# Revit family: Shower-Wall-Bradley_Corp-HN200-VL-SR-SB
name_source: partatom
category: Plumbing Fixtures
revit_build: Autodesk Revit MEP 2012 (Build: 20110309_2315(x64)
units: mm (PartAtom-declared; Revit-internal decimal feet)

## types (86) — shared parameters
ADA Compliant = Yes
Assembly Code = D2010710
Buy American Act = To Be Determined
Cold Water Connection Diameter = 1"
Cold Water Connection Radius = 0"
Depth = 36 "
Description = Recess-Mounted ADA Compliant Wall Shower
Height = 80.627 "
Hot Water Connection Diameter = 1"
Hot Water Connection Radius = 0"
Installation Type = Wall Mounted
Manufacturer = Bradley Corporation
MasterFormat Number = 22 42 23
MasterFormat Title = Commercial Showers
Maximum Operating Pressure = 0.00 psi
Minimum Flow = 0 GPM
OmniClass Table 21 Number = 21-04 20 10 60
OmniClass Table 21 Title = Plumbing Fixtures
OmniClass Table 23 Number = 23-31 17 00
OmniClass Table 23 Title = Showers
Product Tech Data URL - English = http://bradleycorp.com
SVHC = Yes
Seat Material = Plastic - Bradley Corp - Polyethylene - White
Shower Panel Material = Metal - Bradley Corp - Stainless Steel
Showerhead Material = Metal - Bradley Corp - Chrome
Specifications URL = http://www.bradleycorp.com
URL = http://www.bradleycorp.com
Valve Material = Metal - Bradley Corp - Chrome
Version = 2.0
Width = 36 "
zero-valued in all types: CWFU, HWFU, Percentage of Recycled Content

## per-type parameters (varying)
| type | Air Metering Valve | CALC_ASTT | CALC_EqPlate | CALC_EqTMV | Deluxe Showerhead with Ball Joint | Economy Soft Flow Showerhead with Ball Joint | Equa-Flo HD Pressure Balancing Valve | Equa-Flo Pressure Balancing Valve | Infrared Metering Valve | Lockable Ball Joint | Model | Optional 1.5 GPM Flow Control | Recessed Soap Dish | Severe Service Showerhead | Single Compression Valve with Lever Handle | Soap Container in Panel with Liquid Soap Valve | Standard Showerhead | Thermostatic Mixing Valve | TouchTime Metering Valve | Type Comments |
| Hot/Tempered and Cold Supplies | No | No | No | No | No | No | No | No | No | No | - | No | No | No | No | No | No | No | No | - |
| HN200-VL-SR-SB-EF-S-CS | No | No | Yes | No | No | No | No | Yes | No | No | HN200-VL-SR-SB | No | Yes | No | No | Yes | Yes | No | No | Recess-Mounted ADA Compliant Wall Shower with Equa-Flo Pressure Balancing Valve and Standard Showerhead and Soap Container in Panel with Liquid Soap Valve |
| HN200-VL-SR-SB-HD-S-CS | No | No | Yes | Yes | No | No | Yes | No | No | No | HN200-VL-SR-SB | No | Yes | No | No | Yes | Yes | No | No | Recess-Mounted ADA Compliant Wall Shower with Equa-Flo HD Pressure Balancing Valve and Standard Showerhead and Soap Container in Panel with Liquid Soap Valve |
| HN200-VL-SR-SB-TMV-S-CS | No | No | Yes | Yes | No | No | No | No | No | No | HN200-VL-SR-SB | No | Yes | No | No | Yes | Yes | Yes | No | Recess-Mounted ADA Compliant Wall Shower with Thermostatic Mixing Valve and Standard Showerhead and Soap Container in Panel with Liquid Soap Valve |
| HN200-VL-SR-SB-EF-SX-CS | No | No | Yes | No | No | No | No | Yes | No | No | HN200-VL-SR-SB | No | Yes | Yes | No | Yes | No | No | No | Recess-Mounted ADA Compliant Wall Shower with Equa-Flo Pressure Balancing Valve and Severe Service Showerhead and Soap Container in Panel with Liquid Soap Valve |
| HN200-VL-SR-SB-EF-SX-G-CS | No | No | Yes | No | No | No | No | Yes | No | No | HN200-VL-SR-SB | Yes | Yes | Yes | No | Yes | No | No | No | Recess-Mounted ADA Compliant Wall Shower with Equa-Flo Pressure Balancing Valve and Severe Service Showerhead with optional 1.5GPM Flow Control and Soap Container in Panel with Liquid Soap Valve |
| HN200-VL-SR-SB-HD-SX-CS | No | No | Yes | Yes | No | No | Yes | No | No | No | HN200-VL-SR-SB | No | Yes | Yes | No | Yes | No | No | No | Recess-Mounted ADA Compliant Wall Shower with Equa-Flo HD Pressure Balancing Valve and Severe Service Showerhead and Soap Container in Panel with Liquid Soap Valve |
| HN200-VL-SR-SB-HD-SX-G-CS | No | No | Yes | Yes | No | No | Yes | No | No | No | HN200-VL-SR-SB | Yes | Yes | Yes | No | Yes | No | No | No | Recess-Mounted ADA Compliant Wall Shower with Equa-Flo HD Pressure Balancing Valve and Severe Service Showerhead with optional 1.5GPM Flow Control and Soap Container in Panel with Liquid Soap Valve |
| HN200-VL-SR-SB-TMV-SX-CS | No | No | Yes | Yes | No | No | No | No | No | No | HN200-VL-SR-SB | No | Yes | Yes | No | Yes | No | Yes | No | Recess-Mounted ADA Compliant Wall Shower with Thermostatic Mixing Valve and Severe Service Showerhead and Soap Container in Panel with Liquid Soap Valve |
| HN200-VL-SR-SB-TMV-SX-G-CS | No | No | Yes | Yes | No | No | No | No | No | No | HN200-VL-SR-SB | Yes | Yes | Yes | No | Yes | No | Yes | No | Recess-Mounted ADA Compliant Wall Shower with Thermostatic Mixing Valve and Severe Service Showerhead with optional 1.5GPM Flow Control and Soap Container in Panel with Liquid Soap Valve |
| HN200-VL-SR-SB-EF-SF-CS | No | No | Yes | No | Yes | No | No | Yes | No | No | HN200-VL-SR-SB | No | Yes | No | No | Yes | No | No | No | Recess-Mounted ADA Compliant Wall Shower with Equa-Flo Pressure Balancing Valve and Deluxe Showerhead with Ball Joint and Soap Container in Panel with Liquid Soap Valve |
| HN200-VL-SR-SB-EF-SF-LBJ-CS | No | No | Yes | No | Yes | No | No | Yes | No | Yes | HN200-VL-SR-SB | No | Yes | No | No | Yes | No | No | No | Recess-Mounted ADA Compliant Wall Shower with Equa-Flo Pressure Balancing Valve and Deluxe Showerhead with Ball Joint with optional Lockable Ball Joint and Soap Container in Panel with Liquid Soap Valve |
| HN200-VL-SR-SB-HD-SF-CS | No | No | Yes | Yes | Yes | No | Yes | No | No | No | HN200-VL-SR-SB | No | Yes | No | No | Yes | No | No | No | Recess-Mounted ADA Compliant Wall Shower with Equa-Flo HD Pressure Balancing Valve and Deluxe Showerhead with Ball Joint and Soap Container in Panel with Liquid Soap Valve |
| HN200-VL-SR-SB-HD-SF-LBJ-CS | No | No | Yes | Yes | Yes | No | Yes | No | No | Yes | HN200-VL-SR-SB | No | Yes | No | No | Yes | No | No | No | Recess-Mounted ADA Compliant Wall Shower with Equa-Flo HD Pressure Balancing Valve and Deluxe Showerhead with Ball Joint with optional Lockable Ball Joint and Soap Container in Panel with Liquid Soap Valve |
| HN200-VL-SR-SB-TMV-SF-CS | No | No | Yes | Yes | Yes | No | No | No | No | No | HN200-VL-SR-SB | No | Yes | No | No | Yes | No | Yes | No | Recess-Mounted ADA Compliant Wall Shower with Thermostatic Mixing Valve and Deluxe Showerhead with Ball Joint and Soap Container in Panel with Liquid Soap Valve |
| HN200-VL-SR-SB-TMV-SF-LBJ-CS | No | No | Yes | Yes | Yes | No | No | No | No | Yes | HN200-VL-SR-SB | No | Yes | No | No | Yes | No | Yes | No | Recess-Mounted ADA Compliant Wall Shower with Thermostatic Mixing Valve and Deluxe Showerhead with Ball Joint with optional Lockable Ball Joint and Soap Container in Panel with Liquid Soap Valve |
| HN200-VL-SR-SB-EF-ES-CS | No | No | Yes | No | No | Yes | No | Yes | No | No | HN200-VL-SR-SB | No | Yes | No | No | Yes | No | No | No | Recess-Mounted ADA Compliant Wall Shower with Equa-Flo Pressure Balancing Valve and Economy Soft Flow Showerhead with Ball Joint and Soap Container in Panel with Liquid Soap Valve |
| HN200-VL-SR-SB-HD-ES-CS | No | No | Yes | Yes | No | Yes | Yes | No | No | No | HN200-VL-SR-SB | No | Yes | No | No | Yes | No | No | No | Recess-Mounted ADA Compliant Wall Shower with Equa-Flo HD Pressure Balancing Valve and Economy Soft Flow Showerhead with Ball Joint and Soap Container in Panel with Liquid Soap Valve |
| HN200-VL-SR-SB-TMV-ES-CS | No | No | Yes | Yes | No | Yes | No | No | No | No | HN200-VL-SR-SB | No | Yes | No | No | Yes | No | Yes | No | Recess-Mounted ADA Compliant Wall Shower with Thermostatic Mixing Valve and Economy Soft Flow Showerhead with Ball Joint and Soap Container in Panel with Liquid Soap Valve |
| HN200-VL-SR-SB-EF-S | No | No | Yes | No | No | No | No | Yes | No | No | HN200-VL-SR-SB | No | Yes | No | No | No | Yes | No | No | Recess-Mounted ADA Compliant Wall Shower with Equa-Flo Pressure Balancing Valve and Standard Showerhead and Recessed Soap Dish |
| HN200-VL-SR-SB-HD-S | No | No | Yes | Yes | No | No | Yes | No | No | No | HN200-VL-SR-SB | No | Yes | No | No | No | Yes | No | No | Recess-Mounted ADA Compliant Wall Shower with Equa-Flo HD Pressure Balancing Valve and Standard Showerhead and Recessed Soap Dish |
| HN200-VL-SR-SB-TMV-S | No | No | Yes | Yes | No | No | No | No | No | No | HN200-VL-SR-SB | No | Yes | No | No | No | Yes | Yes | No | Recess-Mounted ADA Compliant Wall Shower with Thermostatic Mixing Valve and Standard Showerhead and Recessed Soap Dish |
| HN200-VL-SR-SB-EF-SX | No | No | Yes | No | No | No | No | Yes | No | No | HN200-VL-SR-SB | No | Yes | Yes | No | No | No | No | No | Recess-Mounted ADA Compliant Wall Shower with Equa-Flo Pressure Balancing Valve and Severe Service Showerhead and Recessed Soap Dish |
| HN200-VL-SR-SB-EF-SX-G | No | No | Yes | No | No | No | No | Yes | No | No | HN200-VL-SR-SB | Yes | Yes | Yes | No | No | No | No | No | Recess-Mounted ADA Compliant Wall Shower with Equa-Flo Pressure Balancing Valve and Severe Service Showerhead with optional 1.5GPM Flow Control and Recessed Soap Dish |
| HN200-VL-SR-SB-HD-SX | No | No | Yes | Yes | No | No | Yes | No | No | No | HN200-VL-SR-SB | No | Yes | Yes | No | No | No | No | No | Recess-Mounted ADA Compliant Wall Shower with Equa-Flo HD Pressure Balancing Valve and Severe Service Showerhead and Recessed Soap Dish |
| HN200-VL-SR-SB-HD-SX-G | No | No | Yes | Yes | No | No | Yes | No | No | No | HN200-VL-SR-SB | Yes | Yes | Yes | No | No | No | No | No | Recess-Mounted ADA Compliant Wall Shower with Equa-Flo HD Pressure Balancing Valve and Severe Service Showerhead with optional 1.5GPM Flow Control and Recessed Soap Dish |
| HN200-VL-SR-SB-TMV-SX | No | No | Yes | Yes | No | No | No | No | No | No | HN200-VL-SR-SB | No | Yes | Yes | No | No | No | Yes | No | Recess-Mounted ADA Compliant Wall Shower with Thermostatic Mixing Valve and Severe Service Showerhead and Recessed Soap Dish |
| HN200-VL-SR-SB-TMV-SX-G | No | No | Yes | Yes | No | No | No | No | No | No | HN200-VL-SR-SB | Yes | Yes | Yes | No | No | No | Yes | No | Recess-Mounted ADA Compliant Wall Shower with Thermostatic Mixing Valve and Severe Service Showerhead with optional 1.5GPM Flow Control and Recessed Soap Dish |
| HN200-VL-SR-SB-EF-SF | No | No | Yes | No | Yes | No | No | Yes | No | No | HN200-VL-SR-SB | No | Yes | No | No | No | No | No | No | Recess-Mounted ADA Compliant Wall Shower with Equa-Flo Pressure Balancing Valve and Deluxe Showerhead with Ball Joint and Recessed Soap Dish |
| HN200-VL-SR-SB-EF-SF-LBJ | No | No | Yes | No | Yes | No | No | Yes | No | Yes | HN200-VL-SR-SB | No | Yes | No | No | No | No | No | No | Recess-Mounted ADA Compliant Wall Shower with Equa-Flo Pressure Balancing Valve and Deluxe Showerhead with Ball Joint with optional Lockable Ball Joint and Recessed Soap Dish |
| HN200-VL-SR-SB-HD-SF | No | No | Yes | Yes | Yes | No | Yes | No | No | No | HN200-VL-SR-SB | No | Yes | No | No | No | No | No | No | Recess-Mounted ADA Compliant Wall Shower with Equa-Flo HD Pressure Balancing Valve and Deluxe Showerhead with Ball Joint and Recessed Soap Dish |
| HN200-VL-SR-SB-HD-SF-LBJ | No | No | Yes | Yes | Yes | No | Yes | No | No | Yes | HN200-VL-SR-SB | No | Yes | No | No | No | No | No | No | Recess-Mounted ADA Compliant Wall Shower with Equa-Flo HD Pressure Balancing Valve and Deluxe Showerhead with Ball Joint with optional Lockable Ball Joint and Recessed Soap Dish |
| HN200-VL-SR-SB-TMV-SF | No | No | Yes | Yes | Yes | No | No | No | No | No | HN200-VL-SR-SB | No | Yes | No | No | No | No | Yes | No | Recess-Mounted ADA Compliant Wall Shower with Thermostatic Mixing Valve and Deluxe Showerhead with Ball Joint and Recessed Soap Dish |
| HN200-VL-SR-SB-TMV-SF-LBJ | No | No | Yes | Yes | Yes | No | No | No | No | Yes | HN200-VL-SR-SB | No | Yes | No | No | No | No | Yes | No | Recess-Mounted ADA Compliant Wall Shower with Thermostatic Mixing Valve and Deluxe Showerhead with Ball Joint with optional Lockable Ball Joint and Recessed Soap Dish |
| HN200-VL-SR-SB-EF-ES | No | No | Yes | No | No | Yes | No | Yes | No | No | HN200-VL-SR-SB | No | Yes | No | No | No | No | No | No | Recess-Mounted ADA Compliant Wall Shower with Equa-Flo Pressure Balancing Valve and Economy Soft Flow Showerhead with Ball Joint and Recessed Soap Dish |
| HN200-VL-SR-SB-HD-ES | No | No | Yes | Yes | No | Yes | Yes | No | No | No | HN200-VL-SR-SB | No | Yes | No | No | No | No | No | No | Recess-Mounted ADA Compliant Wall Shower with Equa-Flo HD Pressure Balancing Valve and Economy Soft Flow Showerhead with Ball Joint and Recessed Soap Dish |
| HN200-VL-SR-SB-TMV-ES | No | No | Yes | Yes | No | Yes | No | No | No | No | HN200-VL-SR-SB | No | Yes | No | No | No | No | Yes | No | Recess-Mounted ADA Compliant Wall Shower with Thermostatic Mixing Valve and Economy Soft Flow Showerhead with Ball Joint and Recessed Soap Dish |
| Single Tempered/Cold Supply | No | No | No | No | No | No | No | No | No | No | - | No | No | No | No | No | No | No | No | - |
| HN200-VL-SR-SB-AZ-S-CS | No | No | No | No | No | No | No | No | Yes | No | HN200-VL-SR-SB | No | Yes | No | No | Yes | Yes | No | No | Recess-Mounted ADA Compliant Wall Shower with Infrared Metering Valve and Standard Showerhead and Soap Container in Panel with Liquid Soap Valve |
| HN200-VL-SR-SB-AZ-SX-CS | No | No | No | No | No | No | No | No | Yes | No | HN200-VL-SR-SB | No | Yes | Yes | No | Yes | No | No | No | Recess-Mounted ADA Compliant Wall Shower with Infrared Metering Valve and Severe Service Showerhead and Soap Container in Panel with Liquid Soap Valve |
| HN200-VL-SR-SB-AZ-SX-G-CS | No | No | No | No | No | No | No | No | Yes | No | HN200-VL-SR-SB | Yes | Yes | Yes | No | Yes | No | No | No | Recess-Mounted ADA Compliant Wall Shower with Infrared Metering Valve and Severe Service Showerhead with optional 1.5GPM Flow Control and Soap Container in Panel with Liquid Soap Valve |
| HN200-VL-SR-SB-AZ-SF-CS | No | No | No | No | Yes | No | No | No | Yes | No | HN200-VL-SR-SB | No | Yes | No | No | Yes | No | No | No | Recess-Mounted ADA Compliant Wall Shower with Infrared Metering Valve and Deluxe Showerhead with Ball Joint and Soap Container in Panel with Liquid Soap Valve |
| HN200-VL-SR-SB-AZ-SF-LBJ-CS | No | No | No | No | Yes | No | No | No | Yes | Yes | HN200-VL-SR-SB | No | Yes | No | No | Yes | No | No | No | Recess-Mounted ADA Compliant Wall Shower with Infrared Metering Valve and Deluxe Showerhead with Ball Joint with optional Lockable Ball Joint and Soap Container in Panel with Liquid Soap Valve |
| HN200-VL-SR-SB-AZ-ES-CS | No | No | No | No | No | Yes | No | No | Yes | No | HN200-VL-SR-SB | No | Yes | No | No | Yes | No | No | No | Recess-Mounted ADA Compliant Wall Shower with Infrared Metering Valve and Economy Soft Flow Showerhead with Ball Joint and Soap Container in Panel with Liquid Soap Valve |
| HN200-VL-SR-SB-AST-S-CS | Yes | Yes | No | No | No | No | No | No | No | No | HN200-VL-SR-SB | No | Yes | No | No | Yes | Yes | No | No | Recess-Mounted ADA Compliant Wall Shower with Air Metering Valve and Standard Showerhead and Soap Container in Panel with Liquid Soap Valve |
| HN200-VL-SR-SB-AST-SX-CS | Yes | Yes | No | No | No | No | No | No | No | No | HN200-VL-SR-SB | No | Yes | Yes | No | Yes | No | No | No | Recess-Mounted ADA Compliant Wall Shower with Air Metering Valve and Severe Service Showerhead and Soap Container in Panel with Liquid Soap Valve |
| HN200-VL-SR-SB-AST-SX-G-CS | Yes | Yes | No | No | No | No | No | No | No | No | HN200-VL-SR-SB | Yes | Yes | Yes | No | Yes | No | No | No | Recess-Mounted ADA Compliant Wall Shower with Air Metering Valve and Severe Service Showerhead with optional 1.5GPM Flow Control and Soap Container in Panel with Liquid Soap Valve |
| HN200-VL-SR-SB-AST-SF-CS | Yes | Yes | No | No | Yes | No | No | No | No | No | HN200-VL-SR-SB | No | Yes | No | No | Yes | No | No | No | Recess-Mounted ADA Compliant Wall Shower with Air Metering Valve and Deluxe Showerhead with Ball Joint and Soap Container in Panel with Liquid Soap Valve |
| HN200-VL-SR-SB-AST-SF-LBJ-CS | Yes | Yes | No | No | Yes | No | No | No | No | Yes | HN200-VL-SR-SB | No | Yes | No | No | Yes | No | No | No | Recess-Mounted ADA Compliant Wall Shower with Air Metering Valve and Deluxe Showerhead with Ball Joint with optional Lockable Ball Joint and Soap Container in Panel with Liquid Soap Valve |
| HN200-VL-SR-SB-AST-ES-CS | Yes | Yes | No | No | No | Yes | No | No | No | No | HN200-VL-SR-SB | No | Yes | No | No | Yes | No | No | No | Recess-Mounted ADA Compliant Wall Shower with Air Metering Valve and Economy Soft Flow Showerhead with Ball Joint and Soap Container in Panel with Liquid Soap Valve |
| HN200-VL-SR-SB-SVL-S-CS | No | No | No | No | No | No | No | No | No | No | HN200-VL-SR-SB | No | Yes | No | Yes | Yes | Yes | No | No | Recess-Mounted ADA Compliant Wall Shower with Single Compression Valve and Standard Showerhead and Soap Container in Panel with Liquid Soap Valve |
| HN200-VL-SR-SB-SVL-SX-CS | No | No | No | No | No | No | No | No | No | No | HN200-VL-SR-SB | No | Yes | Yes | Yes | Yes | No | No | No | Recess-Mounted ADA Compliant Wall Shower with Single Compression Valve and Severe Service Showerhead and Soap Container in Panel with Liquid Soap Valve |
| HN200-VL-SR-SB-SVL-SX-G-CS | No | No | No | No | No | No | No | No | No | No | HN200-VL-SR-SB | Yes | Yes | Yes | Yes | Yes | No | No | No | Recess-Mounted ADA Compliant Wall Shower with Single Compression Valve and Severe Service Showerhead with optional 1.5GPM Flow Control and Soap Container in Panel with Liquid Soap Valve |
| HN200-VL-SR-SB-SVL-SF-CS | No | No | No | No | Yes | No | No | No | No | No | HN200-VL-SR-SB | No | Yes | No | Yes | Yes | No | No | No | Recess-Mounted ADA Compliant Wall Shower with Single Compression Valve and Deluxe Showerhead with Ball Joint and Soap Container in Panel with Liquid Soap Valve |
| HN200-VL-SR-SB-SVL-SF-LBJ-CS | No | No | No | No | Yes | No | No | No | No | Yes | HN200-VL-SR-SB | No | Yes | No | Yes | Yes | No | No | No | Recess-Mounted ADA Compliant Wall Shower with Single Compression Valve and Deluxe Showerhead with Ball Joint with optional Lockable Ball Joint and Soap Container in Panel with Liquid Soap Valve |
| HN200-VL-SR-SB-SVL-ES-CS | No | No | No | No | No | Yes | No | No | No | No | HN200-VL-SR-SB | No | Yes | No | Yes | Yes | No | No | No | Recess-Mounted ADA Compliant Wall Shower with Single Compression Valve and Economy Soft Flow Showerhead wiht Ball Joint and Soap Container in Panel with Liquid Soap Valve |
| HN200-VL-SR-SB-TT-S-CS | No | Yes | No | No | No | No | No | No | No | No | HN200-VL-SR-SB | No | Yes | No | No | Yes | Yes | No | Yes | Recess-Mounted ADA Compliant Wall Shower with TouchTime÷ Metering Valve and Standard Showerhead and Soap Container in Panel with Liquid Soap Valve |
| HN200-VL-SR-SB-TT-SX-CS | No | Yes | No | No | No | No | No | No | No | No | HN200-VL-SR-SB | No | Yes | Yes | No | Yes | No | No | Yes | Recess-Mounted ADA Compliant Wall Shower with TouchTime÷ Metering Valve and Severe Service Showerhead and Soap Container in Panel with Liquid Soap Valve |
| HN200-VL-SR-SB-TT-SX-G-CS | No | Yes | No | No | No | No | No | No | No | No | HN200-VL-SR-SB | Yes | Yes | Yes | No | Yes | No | No | Yes | Recess-Mounted ADA Compliant Wall Shower with TouchTime÷ Metering Valve and Severe Service Showerhead with optional 1.5GPM Flow Control and Soap Container in Panel with Liquid Soap Valve |
| HN200-VL-SR-SB-TT-SF-CS | No | Yes | No | No | Yes | No | No | No | No | No | HN200-VL-SR-SB | No | Yes | No | No | Yes | No | No | Yes | Recess-Mounted ADA Compliant Wall Shower with TouchTime÷ Metering Valve and Deluxe Showerhead with Ball Joint and Soap Container in Panel with Liquid Soap Valve |
| HN200-VL-SR-SB-TT-SF-LBJ-CS | No | Yes | No | No | Yes | No | No | No | No | Yes | HN200-VL-SR-SB | No | Yes | No | No | Yes | No | No | Yes | Recess-Mounted ADA Compliant Wall Shower with TouchTime÷ Metering Valve and Deluxe Showerhead with Ball Joint with optional Lockable Ball Joint and Soap Container in Panel with Liquid Soap Valve |
| HN200-VL-SR-SB-TT-ES-CS | No | Yes | No | No | No | Yes | No | No | No | No | HN200-VL-SR-SB | No | Yes | No | No | Yes | No | No | Yes | Recess-Mounted ADA Compliant Wall Shower with TouchTime÷ Metering Valve and Economy Soft Flow Showerhead wiht Ball Joint and Soap Container in Panel with Liquid Soap Valve |
| HN200-VL-SR-SB-AZ-S | No | No | No | No | No | No | No | No | Yes | No | HN200-VL-SR-SB | No | Yes | No | No | No | Yes | No | No | Recess-Mounted ADA Compliant Wall Shower with Infrared Metering Valve and Standard Showerhead and Recessed Soap Dish |
| HN200-VL-SR-SB-AZ-SX | No | No | No | No | No | No | No | No | Yes | No | HN200-VL-SR-SB | No | Yes | Yes | No | No | No | No | No | Recess-Mounted ADA Compliant Wall Shower with Infrared Metering Valve and Severe Service Showerhead and Recessed Soap Dish |
| HN200-VL-SR-SB-AZ-SX-G | No | No | No | No | No | No | No | No | Yes | No | HN200-VL-SR-SB | Yes | Yes | Yes | No | No | No | No | No | Recess-Mounted ADA Compliant Wall Shower with Infrared Metering Valve and Severe Service Showerhead with optional 1.5GPM Flow Control and Recessed Soap Dish |
| HN200-VL-SR-SB-AZ-SF | No | No | No | No | Yes | No | No | No | Yes | No | HN200-VL-SR-SB | No | Yes | No | No | No | No | No | No | Recess-Mounted ADA Compliant Wall Shower with Infrared Metering Valve and Deluxe Showerhead with Ball Joint and Recessed Soap Dish |
| HN200-VL-SR-SB-AZ-SF-LBJ | No | No | No | No | Yes | No | No | No | Yes | Yes | HN200-VL-SR-SB | No | Yes | No | No | No | No | No | No | Recess-Mounted ADA Compliant Wall Shower with Infrared Metering Valve and Deluxe Showerhead with Ball Joint with optional Lockable Ball Joint and Recessed Soap Dish |
| HN200-VL-SR-SB-AZ-ES | No | No | No | No | No | Yes | No | No | Yes | No | HN200-VL-SR-SB | No | Yes | No | No | No | No | No | No | Recess-Mounted ADA Compliant Wall Shower with Infrared Metering Valve and Economy Soft Flow Showerhead with Ball Joint and Recessed Soap Dish |
| HN200-VL-SR-SB-AST-S | Yes | Yes | No | No | No | No | No | No | No | No | HN200-VL-SR-SB | No | Yes | No | No | No | Yes | No | No | Recess-Mounted ADA Compliant Wall Shower with Air Metering Valve and Standard Showerhead and Recessed Soap Dish |
| HN200-VL-SR-SB-AST-SX | Yes | Yes | No | No | No | No | No | No | No | No | HN200-VL-SR-SB | No | Yes | Yes | No | No | No | No | No | Recess-Mounted ADA Compliant Wall Shower with Air Metering Valve and Severe Service Showerhead and Recessed Soap Dish |
| HN200-VL-SR-SB-AST-SX-G | Yes | Yes | No | No | No | No | No | No | No | No | HN200-VL-SR-SB | Yes | Yes | Yes | No | No | No | No | No | Recess-Mounted ADA Compliant Wall Shower with Air Metering Valve and Severe Service Showerhead with optional 1.5GPM Flow Control and Recessed Soap Dish |
| HN200-VL-SR-SB-AST-SF | Yes | Yes | No | No | Yes | No | No | No | No | No | HN200-VL-SR-SB | No | Yes | No | No | No | No | No | No | Recess-Mounted ADA Compliant Wall Shower with Air Metering Valve and Deluxe Showerhead with Ball Joint and Recessed Soap Dish |
| HN200-VL-SR-SB-AST-SF-LBJ | Yes | Yes | No | No | Yes | No | No | No | No | Yes | HN200-VL-SR-SB | No | Yes | No | No | No | No | No | No | Recess-Mounted ADA Compliant Wall Shower with Air Metering Valve and Deluxe Showerhead with Ball Joint with optional Lockable Ball Joint and Recessed Soap Dish |
| HN200-VL-SR-SB-AST-ES | Yes | Yes | No | No | No | Yes | No | No | No | No | HN200-VL-SR-SB | No | Yes | No | No | No | No | No | No | Recess-Mounted ADA Compliant Wall Shower with Air Metering Valve and Economy Soft Flow Showerhead with Ball Joint and Recessed Soap Dish |
| HN200-VL-SR-SB-SVL-S | No | No | No | No | No | No | No | No | No | No | HN200-VL-SR-SB | No | Yes | No | Yes | No | Yes | No | No | Recess-Mounted ADA Compliant Wall Shower with Single Compression Valve and Standard Showerhead and Recessed Soap Dish |
| HN200-VL-SR-SB-SVL-SX | No | No | No | No | No | No | No | No | No | No | HN200-VL-SR-SB | No | Yes | Yes | Yes | No | No | No | No | Recess-Mounted ADA Compliant Wall Shower with Single Compression Valve and Severe Service Showerhead and Recessed Soap Dish |
| HN200-VL-SR-SB-SVL-SX-G | No | No | No | No | No | No | No | No | No | No | HN200-VL-SR-SB | Yes | Yes | Yes | Yes | No | No | No | No | Recess-Mounted ADA Compliant Wall Shower with Single Compression Valve and Severe Service Showerhead with optional 1.5GPM Flow Control and Recessed Soap Dish |
| HN200-VL-SR-SB-SVL-SF | No | No | No | No | Yes | No | No | No | No | No | HN200-VL-SR-SB | No | Yes | No | Yes | No | No | No | No | Recess-Mounted ADA Compliant Wall Shower with Single Compression Valve and Deluxe Showerhead with Ball Joint and Recessed Soap Dish |
| HN200-VL-SR-SB-SVL-SF-LBJ | No | No | No | No | Yes | No | No | No | No | Yes | HN200-VL-SR-SB | No | Yes | No | Yes | No | No | No | No | Recess-Mounted ADA Compliant Wall Shower with Single Compression Valve and Deluxe Showerhead with Ball Joint with optional Lockable Ball Joint and Recessed Soap Dish |
| HN200-VL-SR-SB-SVL-ES | No | No | No | No | No | Yes | No | No | No | No | HN200-VL-SR-SB | No | Yes | No | Yes | No | No | No | No | Recess-Mounted ADA Compliant Wall Shower with Single Compression Valve and Economy Soft Flow Showerhead wiht Ball Joint and Recessed Soap Dish |
| HN200-VL-SR-SB-TT-S | No | Yes | No | No | No | No | No | No | No | No | HN200-VL-SR-SB | No | Yes | No | No | No | Yes | No | Yes | Recess-Mounted ADA Compliant Wall Shower with TouchTime÷ Metering Valve and Standard Showerhead and Recessed Soap Dish |
| HN200-VL-SR-SB-TT-SX | No | Yes | No | No | No | No | No | No | No | No | HN200-VL-SR-SB | No | Yes | Yes | No | No | No | No | Yes | Recess-Mounted ADA Compliant Wall Shower with TouchTime÷ Metering Valve and Severe Service Showerhead and Recessed Soap Dish |
| HN200-VL-SR-SB-TT-SX-G | No | Yes | No | No | No | No | No | No | No | No | HN200-VL-SR-SB | Yes | Yes | Yes | No | No | No | No | Yes | Recess-Mounted ADA Compliant Wall Shower with TouchTime÷ Metering Valve and Severe Service Showerhead with optional 1.5GPM Flow Control and Recessed Soap Dish |
| HN200-VL-SR-SB-TT-SF | No | Yes | No | No | Yes | No | No | No | No | No | HN200-VL-SR-SB | No | Yes | No | No | No | No | No | Yes | Recess-Mounted ADA Compliant Wall Shower with TouchTime÷ Metering Valve and Deluxe Showerhead with Ball Joint and Recessed Soap Dish |
| HN200-VL-SR-SB-TT-SF-LBJ | No | Yes | No | No | Yes | No | No | No | No | Yes | HN200-VL-SR-SB | No | Yes | No | No | No | No | No | Yes | Recess-Mounted ADA Compliant Wall Shower with TouchTime÷ Metering Valve and Deluxe Showerhead with Ball Joint with optional Lockable Ball Joint and Recessed Soap Dish |
| HN200-VL-SR-SB-TT-ES | No | Yes | No | No | No | Yes | No | No | No | No | HN200-VL-SR-SB | No | Yes | No | No | No | No | No | Yes | Recess-Mounted ADA Compliant Wall Shower with TouchTime÷ Metering Valve and Economy Soft Flow Showerhead wiht Ball Joint and Recessed Soap Dish |

## geometry (parser evidence)
native form markers: Blend x8, Sweep x8
no freeform markers — native parametric forms only
